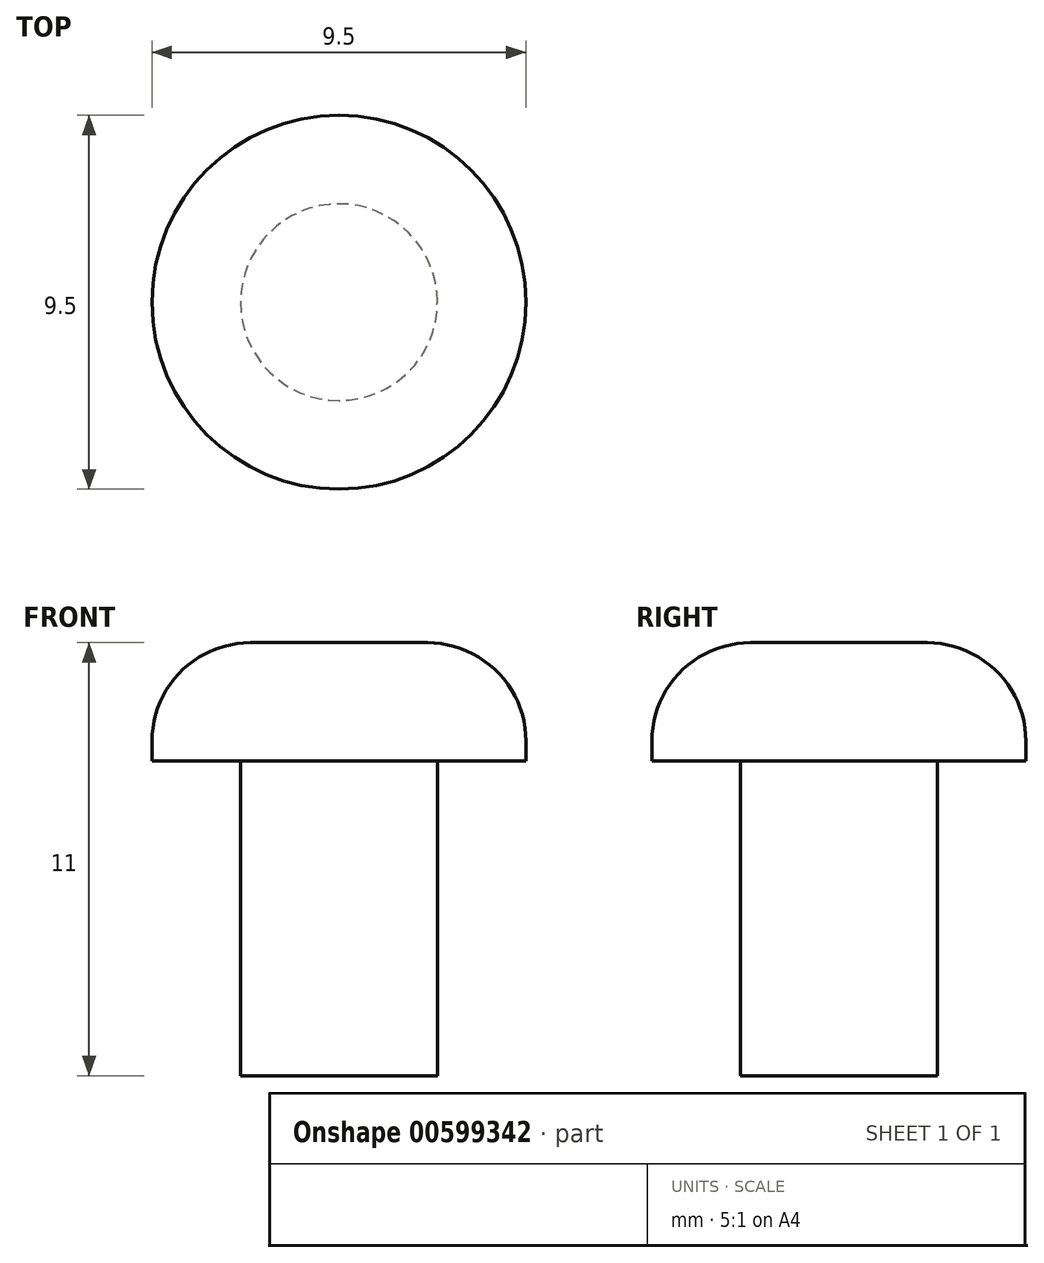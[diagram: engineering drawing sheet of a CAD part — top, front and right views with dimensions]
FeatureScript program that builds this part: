
annotation { "Feature Type Name" : "Feature", "Feature Type Description" : "" }
export const myFeature = defineFeature(function(context is Context, id is Id, definition is map)
    precondition{}
    {
        {
            var Q0;
            Q0=qCreatedBy(makeId("Top.planeOp"),FACE);
            var sketch = newSketch(context, id + "F0", { "sketchPlane" : qUnion([Q0])});
            skCircle(sketch, "E0", {"center": v(0, 0) * mm, "radius": 4.75 * mm});
            skSolve(sketch);
        }
        {
            var Q0;
            Q0=qSketchRegion(id+"F0",true);
            extrude(context, id + "F1", {"entities" : qUnion([Q0]), "depth" : 3 * mm});
        }
        {
            var Q0;
            Q0=makeQuery(id+"F1.opExtrude","CAP_EDGE",EDGE,{"disambiguationData":[OSD([sQuery(id+"F0.wireOp",EDGE,"E0")])],"isStart":false});
            fillet(context, id + "F2", {"entities" : qUnion([Q0]), "radius" : 2.5 * mm, "tangentPropagation" : true, "allowEdgeOverflow" : false});
        }
        {
            var Q0;
            Q0=qCreatedBy(makeId("Top.planeOp"),FACE);
            var sketch = newSketch(context, id + "F3", { "sketchPlane" : qUnion([Q0])});
            skCircle(sketch, "E1", {"center": v(0, 0) * mm, "radius": 2.5 * mm});
            skSolve(sketch);
        }
        {
            var Q0;
            Q0=qSketchRegion(id+"F3",true);
            extrude(context, id + "F4", {"entities" : qUnion([Q0]), "operationType" : NewBodyOperationType.ADD, "oppositeDirection" : true, "depth" : 8 * mm});
        }
    });
